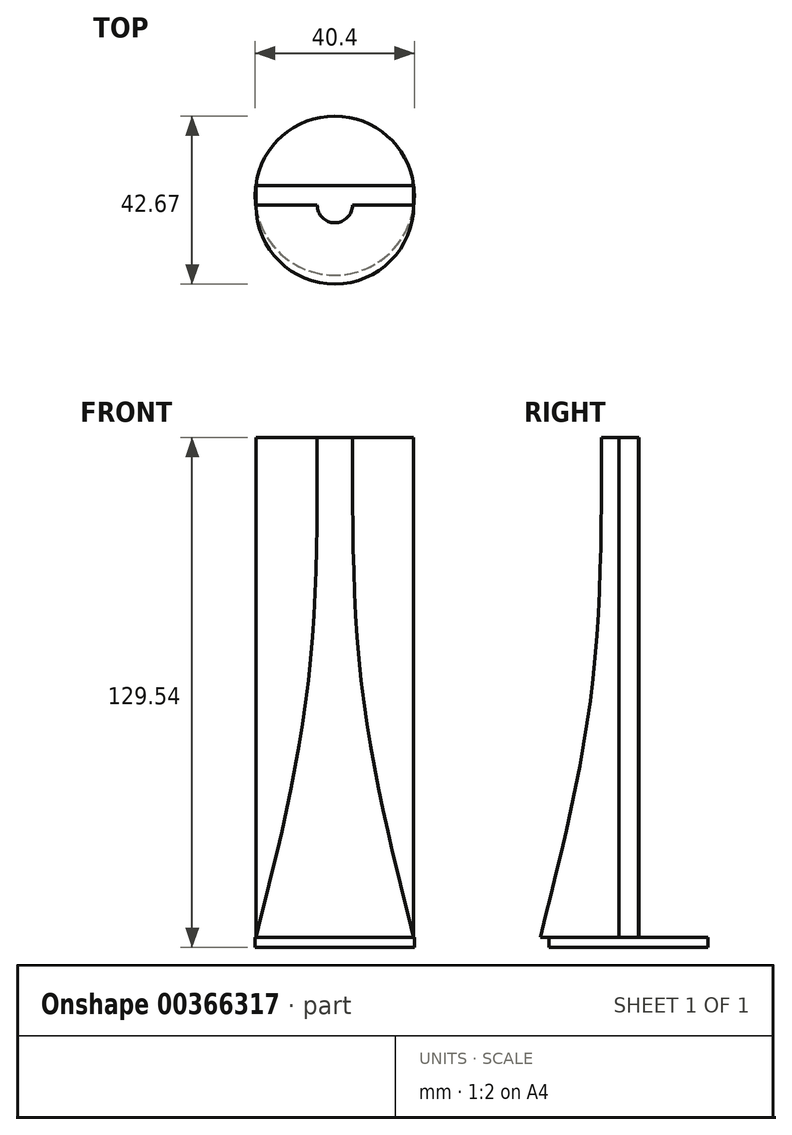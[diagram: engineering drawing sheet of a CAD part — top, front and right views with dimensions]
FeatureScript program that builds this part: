
annotation { "Feature Type Name" : "Feature", "Feature Type Description" : "" }
export const myFeature = defineFeature(function(context is Context, id is Id, definition is map)
    precondition{}
    {
        {
            var Q0;
            Q0=qCreatedBy(makeId("Top.planeOp"),FACE);
            var sketch = newSketch(context, id + "F0", { "sketchPlane" : qUnion([Q0])});
            skCircle(sketch, "E0", {"center": v(0, 0) * mm, "radius": 20.2 * mm});
            skSolve(sketch);
        }
        {
            var Q0;
            Q0=makeQuery(id+"F0.imprint","IMPRINT",FACE,{"disambiguationData":[TD([[makeQuery(id+"F0.imprint","IMPRINT",EDGE,{"derivedFrom":sQuery(id+"F0.wireOp",EDGE,"E0")}),1.0]])]});
            extrude(context, id + "F1", {"entities" : qUnion([Q0]), "depth" : 2.54 * mm});
        }
        {
            var Q0;
            Q0=makeQuery(id+"F1.opExtrude","CAP_FACE",FACE,{"disambiguationData":[OSD([sQuery(id+"F0.wireOp",EDGE,"E0")])],"isStart":false});
            var sketch = newSketch(context, id + "F2", { "sketchPlane" : qUnion([Q0])});
            skLineSegment(sketch, "E1.bottom", {"start": v(-20.03, 2.6) * mm, "end": v(20.06, 2.6) * mm});
            skLineSegment(sketch, "E1.top", {"start": v(-20.03, -2.42) * mm, "end": v(20.06, -2.42) * mm});
            skLineSegment(sketch, "E1.left", {"start": v(-20.03, 2.6) * mm, "end": v(-20.03, -2.42) * mm});
            skLineSegment(sketch, "E1.right", {"start": v(20.06, 2.6) * mm, "end": v(20.06, -2.42) * mm});
            skSolve(sketch);
        }
        {
            var Q0;
            {var subQ1=sQuery(id+"F2.wireOp",EDGE,"E1.top");Q0=makeQuery(id+"F2.imprint","IMPRINT",FACE,{"disambiguationData":[TD([[makeQuery(id+"F2.imprint","IMPRINT",EDGE,{"derivedFrom":subQ1}),1.0]])]});}
            extrude(context, id + "F3", {"entities" : qUnion([Q0]), "operationType" : NewBodyOperationType.ADD, "depth" : 127 * mm});
        }
        {
            var Q0;
            Q0=makeQuery(id+"F3.opExtrude","SWEPT_FACE",FACE,{"disambiguationData":[OSD([sQuery(id+"F2.wireOp",EDGE,"E1.top")])]});
            var sketch = newSketch(context, id + "F4", { "sketchPlane" : qUnion([Q0])});
            skLineSegment(sketch, "E2.bottom", {"start": v(0.01, 2.54) * mm, "end": v(20.06, 2.54) * mm});
            skLineSegment(sketch, "E2.top", {"start": v(0.01, 129.54) * mm, "end": v(20.06, 129.54) * mm});
            skLineSegment(sketch, "E2.left", {"start": v(0.01, 2.54) * mm, "end": v(0.01, 129.54) * mm});
            skLineSegment(sketch, "E2.right", {"start": v(20.06, 2.54) * mm, "end": v(20.06, 129.54) * mm});
            skFitSpline(sketch, "E3", {"points": [v(20.06, 2.54) * mm, v(7.1, 64.66) * mm, v(4.48, 129.54) * mm], "startDerivative": vector(-31.26, 123.94) * mm, "endDerivative": vector(0.06, 130.04) * mm});
            skSolve(sketch);
        }
        {
            var Q0;
            Q0=makeQuery(id+"F4.imprint","IMPRINT",FACE,{"disambiguationData":[TD([[makeQuery(id+"F4.imprint","IMPRINT",EDGE,{"derivedFrom":sQuery(id+"F4.wireOp",EDGE,"E2.bottom")}),1.0]])]});
            var Q1;
            Q1=sQuery(id+"F4.wireOp",EDGE,"E2.left");
            revolve(context, id + "F5", {"operationType" : NewBodyOperationType.ADD, "entities" : qUnion([Q0]), "axis" : qUnion([Q1]), "revolveType" : RevolveType.ONE_DIRECTION, "oppositeDirection" : true, "angle" : 180 * degree});
        }
    });
